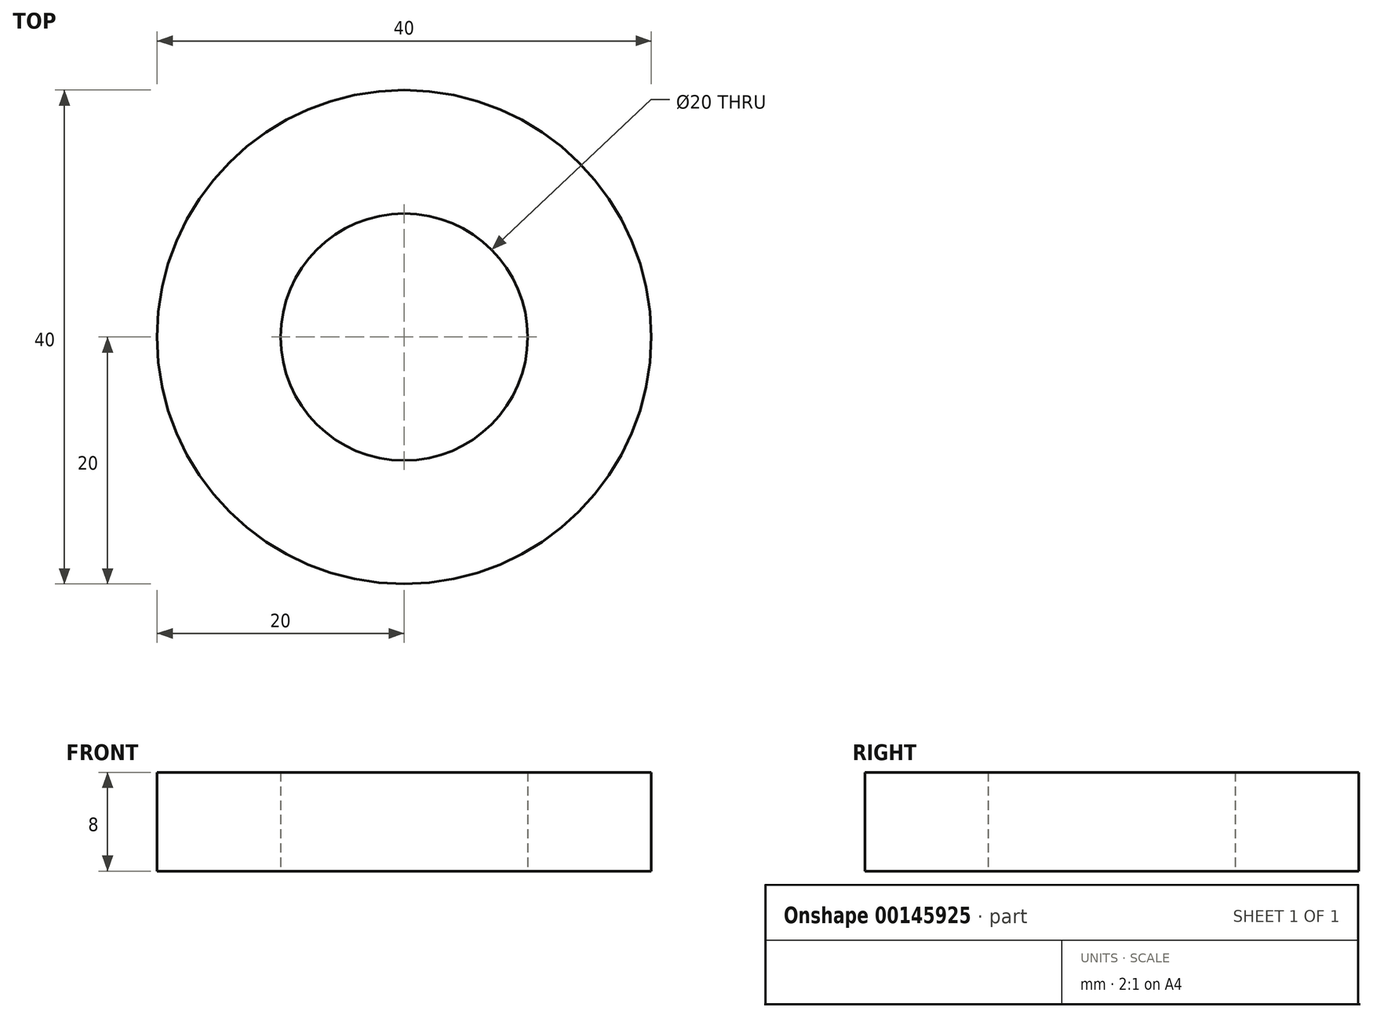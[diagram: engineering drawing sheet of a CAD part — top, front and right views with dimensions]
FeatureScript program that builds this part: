
annotation { "Feature Type Name" : "Feature", "Feature Type Description" : "" }
export const myFeature = defineFeature(function(context is Context, id is Id, definition is map)
    precondition{}
    {
        {
            var Q0;
            Q0=qCreatedBy(makeId("Top.planeOp"),FACE);
            var sketch = newSketch(context, id + "F0", { "sketchPlane" : qUnion([Q0])});
            skCircle(sketch, "E0", {"center": v(0, 0) * mm, "radius": 10 * mm});
            skCircle(sketch, "E1", {"center": v(0, 0) * mm, "radius": 20 * mm});
            skSolve(sketch);
        }
        {
            var Q0;
            Q0=makeQuery(id+"F0.imprint","IMPRINT",FACE,{"disambiguationData":[TD([[makeQuery(id+"F0.imprint","IMPRINT",EDGE,{"derivedFrom":sQuery(id+"F0.wireOp",EDGE,"E0")}),-1.0]])]});
            extrude(context, id + "F1", {"entities" : qUnion([Q0]), "depth" : 8 * mm});
        }
    });
